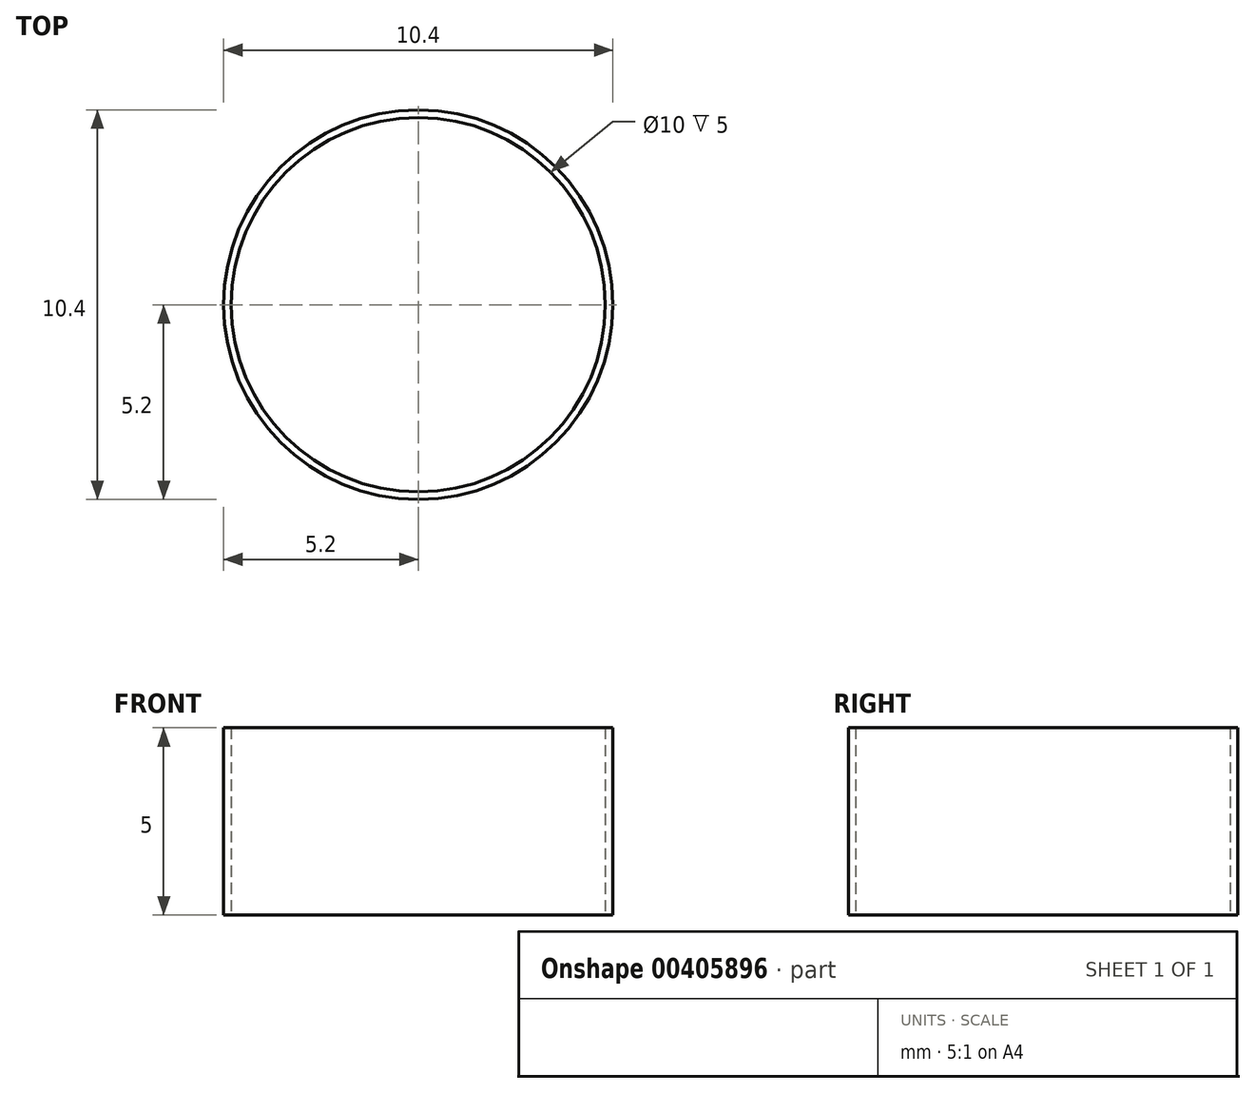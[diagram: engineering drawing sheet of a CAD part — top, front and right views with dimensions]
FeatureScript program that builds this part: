
annotation { "Feature Type Name" : "Feature", "Feature Type Description" : "" }
export const myFeature = defineFeature(function(context is Context, id is Id, definition is map)
    precondition{}
    {
        {
            var Q0;
            Q0=qCreatedBy(makeId("Top.planeOp"),FACE);
            var sketch = newSketch(context, id + "F0", { "sketchPlane" : qUnion([Q0])});
            skCircle(sketch, "E0", {"center": v(0, 0) * mm, "radius": 5 * mm});
            skCircle(sketch, "E1.0", {"center": v(0, 0) * mm, "radius": 5.2 * mm});
            skSolve(sketch);
        }
        {
            var Q0;
            Q0=makeQuery(id+"F0.imprint","IMPRINT",FACE,{"disambiguationData":[TD([[makeQuery(id+"F0.imprint","IMPRINT",EDGE,{"derivedFrom":sQuery(id+"F0.wireOp",EDGE,"E0")}),-1.0]])]});
            extrude(context, id + "F1", {"entities" : qUnion([Q0]), "depth" : 5 * mm});
        }
    });
